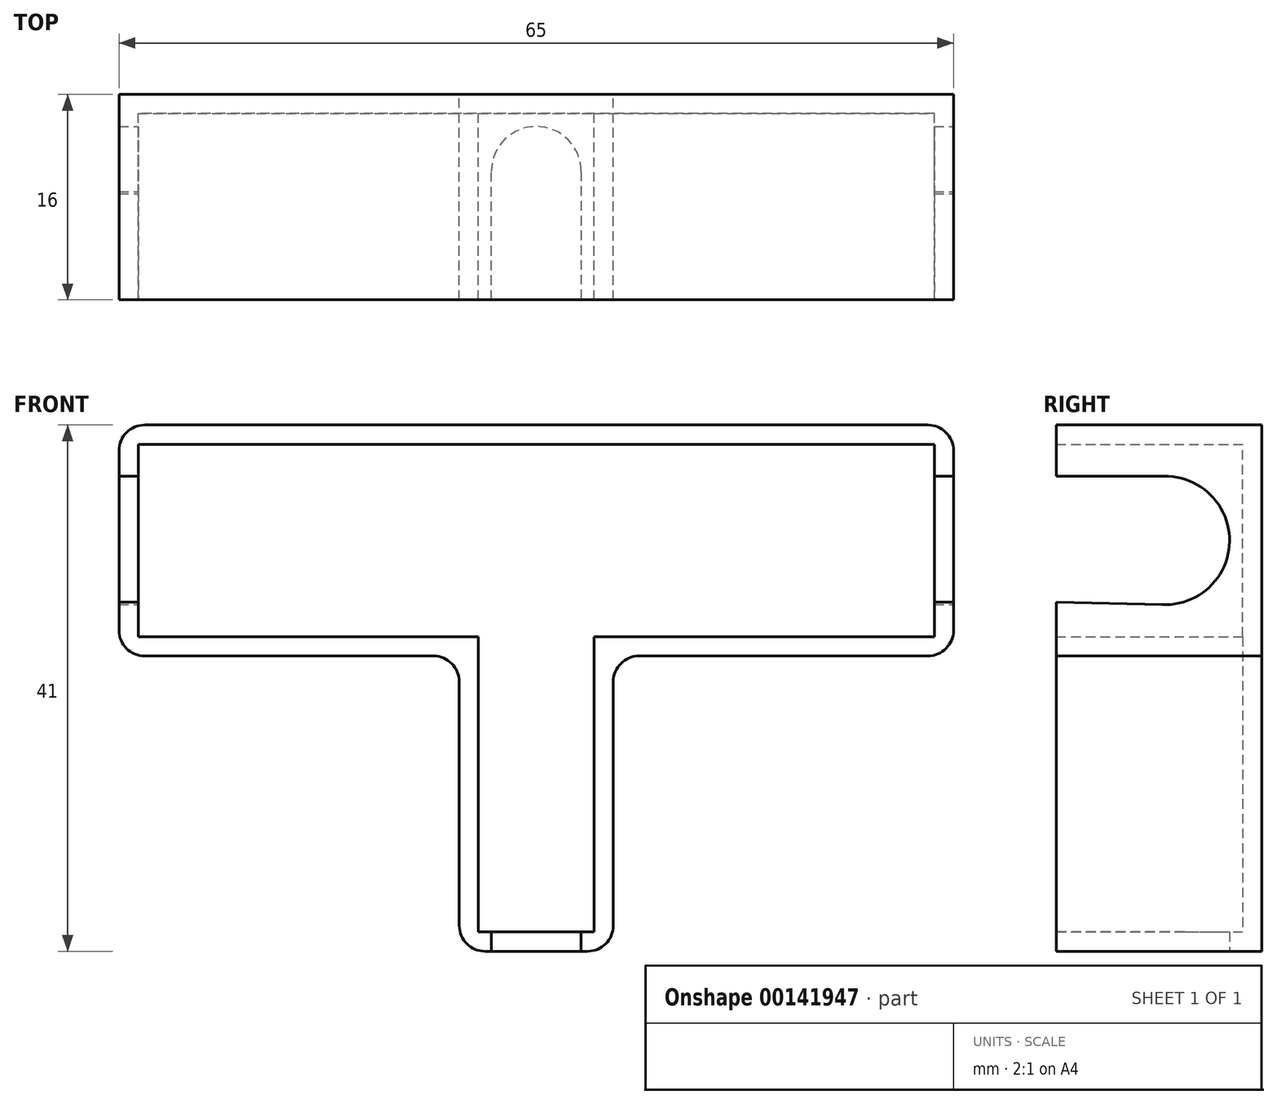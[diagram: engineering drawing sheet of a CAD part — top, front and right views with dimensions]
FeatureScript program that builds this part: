
annotation { "Feature Type Name" : "Feature", "Feature Type Description" : "" }
export const myFeature = defineFeature(function(context is Context, id is Id, definition is map)
    precondition{}
    {
        {
            var Q0;
            Q0=qCreatedBy(makeId("Front.planeOp"),FACE);
            var sketch = newSketch(context, id + "F0", { "sketchPlane" : qUnion([Q0])});
            skLineSegment(sketch, "E0", {"start": v(32.5, 9) * mm, "end": v(-32.5, 9) * mm});
            skLineSegment(sketch, "E1", {"start": v(-32.5, 9) * mm, "end": v(-32.5, -9) * mm});
            skLineSegment(sketch, "E2", {"start": v(-32.5, -9) * mm, "end": v(-6, -9) * mm});
            skLineSegment(sketch, "E3", {"start": v(-6, -9) * mm, "end": v(-6, -32) * mm});
            skLineSegment(sketch, "E4", {"start": v(-6, -32) * mm, "end": v(6, -32) * mm});
            skLineSegment(sketch, "E5", {"start": v(6, -32) * mm, "end": v(6, -9) * mm});
            skLineSegment(sketch, "E6", {"start": v(6, -9) * mm, "end": v(32.5, -9) * mm});
            skLineSegment(sketch, "E7", {"start": v(32.5, -9) * mm, "end": v(32.5, 9) * mm});
            skSolve(sketch);
        }
        {
            var Q0;
            Q0=makeQuery(id+"F0.imprint","IMPRINT",FACE,{"disambiguationData":[TD([[makeQuery(id+"F0.imprint","IMPRINT",EDGE,{"derivedFrom":sQuery(id+"F0.wireOp",EDGE,"E0")}),1.0]])]});
            extrude(context, id + "F1", {"entities" : qUnion([Q0]), "depth" : 16 * mm, "offsetDistance" : 25 * mm});
        }
        {
            var Q0;
            Q0=makeQuery(id+"F1.opExtrude","CAP_FACE",FACE,{"disambiguationData":[OSD([sQuery(id+"F0.wireOp",EDGE,"E0"),sQuery(id+"F0.wireOp",EDGE,"E1"),sQuery(id+"F0.wireOp",EDGE,"E2"),sQuery(id+"F0.wireOp",EDGE,"E3"),sQuery(id+"F0.wireOp",EDGE,"E4"),sQuery(id+"F0.wireOp",EDGE,"E5"),sQuery(id+"F0.wireOp",EDGE,"E6"),sQuery(id+"F0.wireOp",EDGE,"E7")])],"isStart":false});
            shell(context, id + "F2", {"entities" : qUnion([Q0]), "thickness" : 1.5 * mm});
        }
        {
            var Q0;
            Q0=makeQuery(id+"F1.opExtrude","SWEPT_FACE",FACE,{"disambiguationData":[OSD([sQuery(id+"F0.wireOp",EDGE,"E7")])]});
            var sketch = newSketch(context, id + "F3", { "sketchPlane" : qUnion([Q0])});
            skCircle(sketch, "E8", {"center": v(-7.5, 0) * mm, "radius": 5 * mm});
            skLineSegment(sketch, "E9", {"start": v(-7.41, 5) * mm, "end": v(-16, 5) * mm});
            skLineSegment(sketch, "E10", {"start": v(-16, 5) * mm, "end": v(-16, -4.8) * mm});
            skLineSegment(sketch, "E11", {"start": v(-16, -4.8) * mm, "end": v(-7.5, -5) * mm});
            skSolve(sketch);
        }
        {
            var Q0;
            Q0 = qSketchRegion(id + "F3", true);
            extrude(context, id + "F4", {"entities" : qUnion([Q0]), "operationType" : NewBodyOperationType.REMOVE, "oppositeDirection" : true, "depth" : 100 * mm, "offsetDistance" : 25 * mm});
        }
        {
            var Q0;
            Q0=makeQuery(id+"F1.opExtrude","SWEPT_FACE",FACE,{"disambiguationData":[OSD([sQuery(id+"F0.wireOp",EDGE,"E4")])]});
            var sketch = newSketch(context, id + "F5", { "sketchPlane" : qUnion([Q0])});
            skCircle(sketch, "E12", {"center": v(0, 6) * mm, "radius": 3.5 * mm});
            skLineSegment(sketch, "E13", {"start": v(-3.5, 6) * mm, "end": v(-3.5, 16) * mm});
            skLineSegment(sketch, "E14", {"start": v(-3.5, 16) * mm, "end": v(3.5, 16) * mm});
            skLineSegment(sketch, "E15", {"start": v(3.5, 16) * mm, "end": v(3.5, 3.53) * mm});
            skSolve(sketch);
        }
        {
            var Q0;
            {var subQ0=sQuery(id+"F5.wireOp",EDGE,"E12");var subQ1=makeQuery(id+"F5.imprint","INTERSECT",VERTEX,{"derivedFrom":[subQ0,sQuery(id+"F5.wireOp",EDGE,"E13")]});Q0=makeQuery(id+"F5.imprint","IMPRINT",FACE,{"disambiguationData":[TD([[makeQuery(id+"F5.imprint","IMPRINT",EDGE,{"disambiguationData":[TD([[subQ1,1.0]])],"derivedFrom":subQ0}),1.0]])]});}
            var Q1;
            {var subQ0=sQuery(id+"F5.wireOp",EDGE,"E13");Q1=makeQuery(id+"F5.imprint","IMPRINT",FACE,{"disambiguationData":[TD([[makeQuery(id+"F5.imprint","IMPRINT",EDGE,{"derivedFrom":subQ0}),-1.0]])]});}
            extrude(context, id + "F6", {"entities" : qUnion([Q0, Q1]), "operationType" : NewBodyOperationType.REMOVE, "oppositeDirection" : true, "depth" : 25 * mm, "offsetDistance" : 25 * mm});
        }
        {
            var Q0;
            Q0=makeQuery(id+"F1.opExtrude","SWEPT_EDGE",EDGE,{"disambiguationData":[OSD([sQuery(id+"F0.wireOp",EDGE,"E1"),sQuery(id+"F0.wireOp",EDGE,"E2")])]});
            var Q1;
            Q1=makeQuery(id+"F1.opExtrude","SWEPT_EDGE",EDGE,{"disambiguationData":[OSD([sQuery(id+"F0.wireOp",EDGE,"E2"),sQuery(id+"F0.wireOp",EDGE,"E3")])]});
            var Q2;
            Q2=makeQuery(id+"F1.opExtrude","SWEPT_EDGE",EDGE,{"disambiguationData":[OSD([sQuery(id+"F0.wireOp",EDGE,"E3"),sQuery(id+"F0.wireOp",EDGE,"E4")])]});
            var Q3;
            Q3=makeQuery(id+"F1.opExtrude","SWEPT_EDGE",EDGE,{"disambiguationData":[OSD([sQuery(id+"F0.wireOp",EDGE,"E4"),sQuery(id+"F0.wireOp",EDGE,"E5")])]});
            var Q4;
            Q4=makeQuery(id+"F1.opExtrude","SWEPT_EDGE",EDGE,{"disambiguationData":[OSD([sQuery(id+"F0.wireOp",EDGE,"E5"),sQuery(id+"F0.wireOp",EDGE,"E6")])]});
            var Q5;
            Q5=makeQuery(id+"F1.opExtrude","SWEPT_EDGE",EDGE,{"disambiguationData":[OSD([sQuery(id+"F0.wireOp",EDGE,"E6"),sQuery(id+"F0.wireOp",EDGE,"E7")])]});
            var Q6;
            Q6=makeQuery(id+"F1.opExtrude","SWEPT_EDGE",EDGE,{"disambiguationData":[OSD([sQuery(id+"F0.wireOp",EDGE,"E0"),sQuery(id+"F0.wireOp",EDGE,"E7")])]});
            var Q7;
            Q7=makeQuery(id+"F1.opExtrude","SWEPT_EDGE",EDGE,{"disambiguationData":[OSD([sQuery(id+"F0.wireOp",EDGE,"E0"),sQuery(id+"F0.wireOp",EDGE,"E1")])]});
            fillet(context, id + "F7", {"entities" : qUnion([Q0, Q1, Q2, Q3, Q4, Q5, Q6, Q7]), "radius" : 2 * mm, "tangentPropagation" : true, "allowEdgeOverflow" : false});
        }
    });
